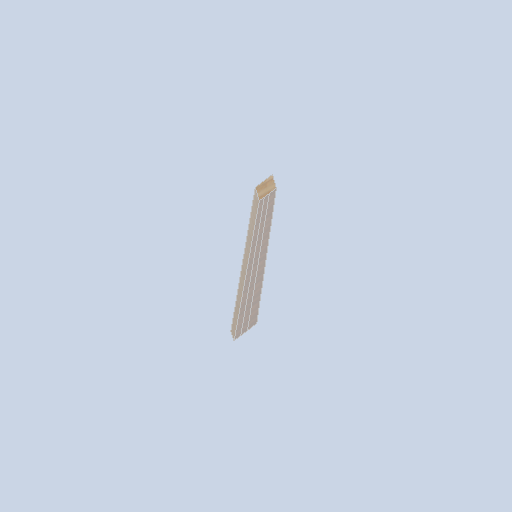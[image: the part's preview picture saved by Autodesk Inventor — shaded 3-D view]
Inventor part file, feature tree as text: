
AUTODESK INVENTOR PART (.ipt)
format: ipt  version: 2024.2 (Build 282272000, 272)  size: 121,344 bytes
history: native  units: in
note: dims shown in document units (in); Inventor stores cm internally (conversion verified against a paired STEP export)
features: sketch x4, other x3, plane x2
ambient origin geometry x8: Origin, YZ Plane, XZ Plane, XY Plane, X Axis, Y Axis, Z Axis, Center Point
bodies: Solid1 (feature_tree)
feature tree (9):
  other  "side_curve_beam_03.ipt"
  other  "Solid1::side_curve_beam_03.ipt"
  other  "TaggingFeature1"
  sketch  "Sketch1"  dims[d0=0.3937in]
  sketch  "Sketch2"
  sketch  "Sketch3"
  sketch  "Sketch4"
  plane  "Work Plane1"
  plane  "Work Plane2"
